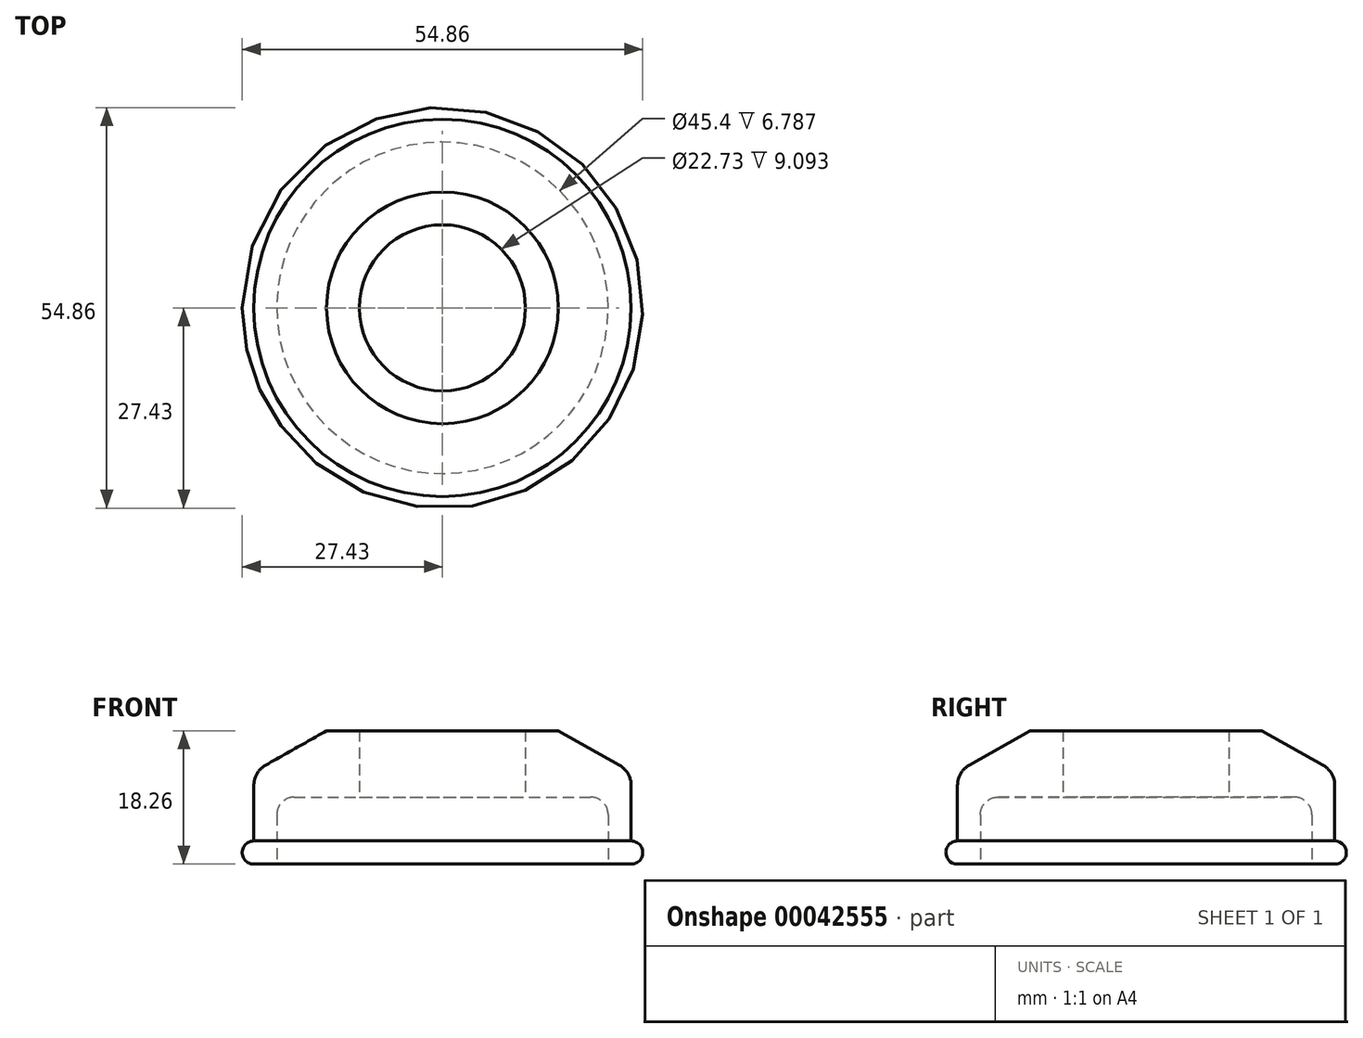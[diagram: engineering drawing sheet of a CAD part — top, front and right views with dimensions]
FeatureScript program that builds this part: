
annotation { "Feature Type Name" : "Feature", "Feature Type Description" : "" }
export const myFeature = defineFeature(function(context is Context, id is Id, definition is map)
    precondition{}
    {
        {
            var Q0;
            Q0=qCreatedBy(makeId("Front.planeOp"),FACE);
            var sketch = newSketch(context, id + "F0", { "sketchPlane" : qUnion([Q0])});
            skLineSegment(sketch, "E0", {"start": v(0, 0) * mm, "end": v(0, 25.56) * mm, "construction": true});
            skLineSegment(sketch, "E1", {"start": v(22.7, 0) * mm, "end": v(22.7, 6.79) * mm});
            skLineSegment(sketch, "E2", {"start": v(20.32, 9.17) * mm, "end": v(11.37, 9.17) * mm});
            skLineSegment(sketch, "E3", {"start": v(11.37, 9.17) * mm, "end": v(11.37, 18.26) * mm});
            skLineSegment(sketch, "E4", {"start": v(11.37, 18.26) * mm, "end": v(15.88, 18.26) * mm});
            skLineSegment(sketch, "E5", {"start": v(15.87, 18.26) * mm, "end": v(24.23, 13.56) * mm});
            skLineSegment(sketch, "E6", {"start": v(25.84, 10.8) * mm, "end": v(25.84, 3.18) * mm});
            skLineSegment(sketch, "E7", {"start": v(22.7, 0) * mm, "end": v(25.84, 0) * mm});
            skArc(sketch, "E8", {"start": v(25.84, 0) * mm, "mid": v(27.43, 1.59) * mm, "end": v(25.84, 3.18) * mm});
            skPoint(sketch, "E9.visualSharp", {"position": v(22.7, 9.17) * mm});
            skArc(sketch, "E9.filletArc", {"start": v(22.7, 6.79) * mm, "mid": v(22, 8.47) * mm, "end": v(20.32, 9.17) * mm});
            skPoint(sketch, "E10.visualSharp", {"position": v(25.84, 12.65) * mm});
            skArc(sketch, "E10.filletArc", {"start": v(25.84, 10.8) * mm, "mid": v(25.41, 12.4) * mm, "end": v(24.23, 13.56) * mm});
            skSolve(sketch);
        }
        {
            var Q0;
            Q0=makeQuery(id+"F0.imprint","IMPRINT",FACE,{"disambiguationData":[TD([[makeQuery(id+"F0.imprint","IMPRINT",EDGE,{"derivedFrom":sQuery(id+"F0.wireOp",EDGE,"E1")}),-1.0]])]});
            var Q1;
            Q1=sQuery(id+"F0.wireOp",EDGE,"E0");
            revolve(context, id + "F1", {"entities" : qUnion([Q0]), "axis" : qUnion([Q1]), "revolveType" : RevolveType.FULL});
        }
    });
